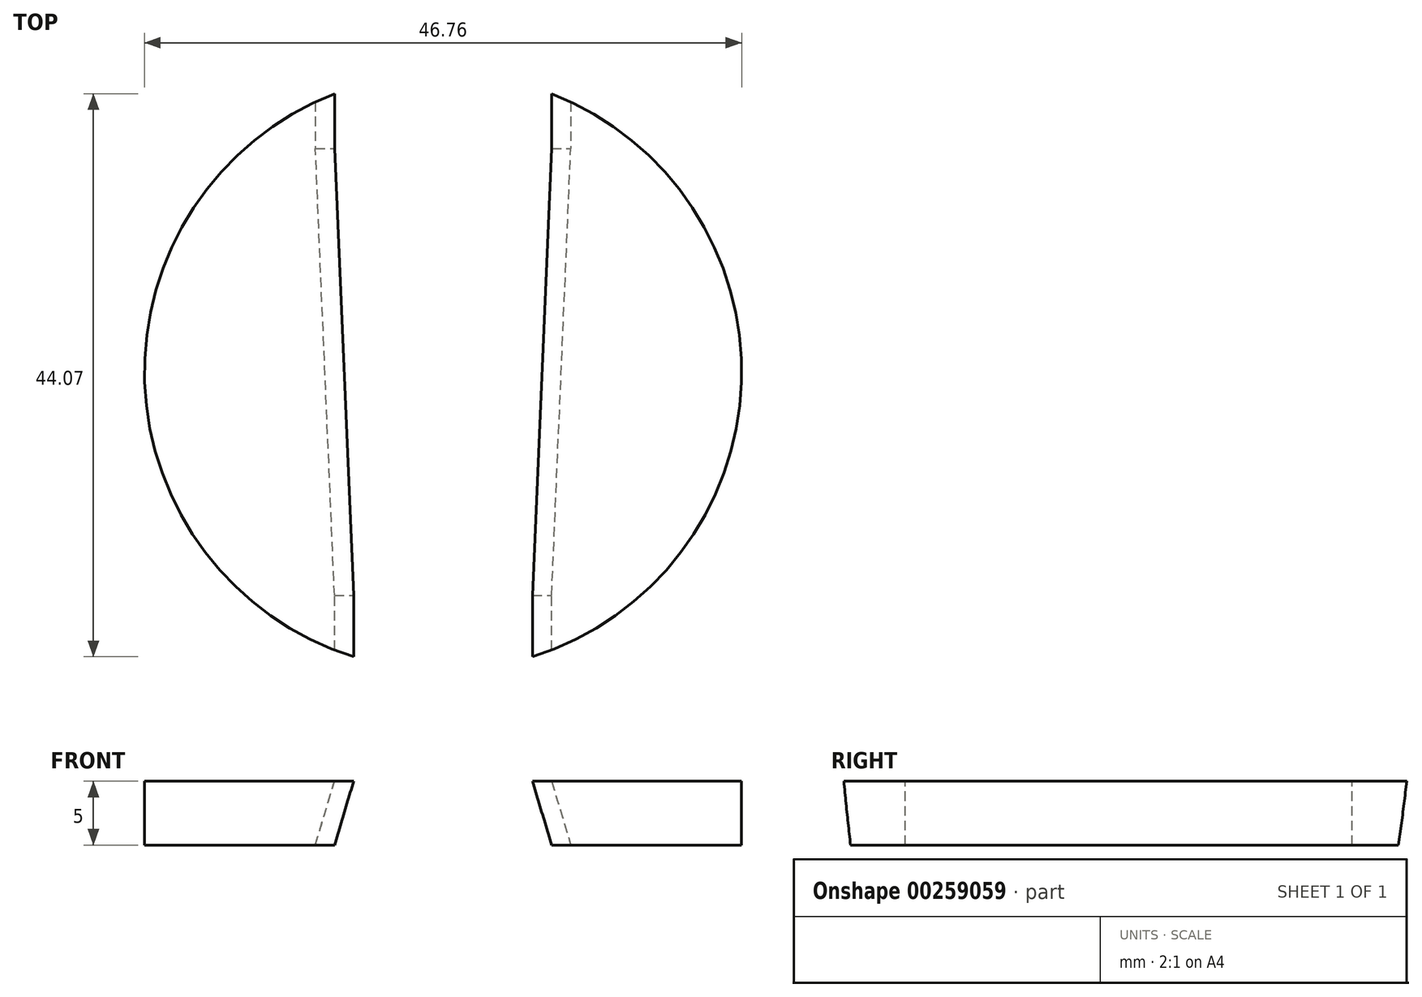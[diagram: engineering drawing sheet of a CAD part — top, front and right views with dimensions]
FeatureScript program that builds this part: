
annotation { "Feature Type Name" : "Feature", "Feature Type Description" : "" }
export const myFeature = defineFeature(function(context is Context, id is Id, definition is map)
    precondition{}
    {
        {
            var Q0;
            Q0=qCreatedBy(makeId("Top.planeOp"),FACE);
            var sketch = newSketch(context, id + "F0", { "sketchPlane" : qUnion([Q0])});
            skCircle(sketch, "E0", {"center": v(0, 0) * mm, "radius": 23.38 * mm});
            skSolve(sketch);
        }
        {
            var Q0;
            Q0=makeQuery(id+"F0.imprint","IMPRINT",FACE,{"disambiguationData":[TD([[makeQuery(id+"F0.imprint","IMPRINT",EDGE,{"derivedFrom":sQuery(id+"F0.wireOp",EDGE,"E0")}),1.0]])]});
            extrude(context, id + "F1", {"entities" : qUnion([Q0]), "depth" : 5 * mm, "offsetDistance" : 25 * mm});
        }
        {
            var Q0;
            Q0=qCreatedBy(makeId("Front.planeOp"),FACE);
            cPlane(context, id + "F2", {"entities" : qUnion([Q0]), "cplaneType" : CPlaneType.OFFSET, "offset" : (35 / 2) * mm, "width" : 150 * mm, "height" : 150 * mm});
        }
        {
            var Q0;
            Q0=qCreatedBy(makeId("Front.planeOp"),FACE);
            cPlane(context, id + "F3", {"entities" : qUnion([Q0]), "cplaneType" : CPlaneType.OFFSET, "offset" : (35 / 2) * mm, "oppositeDirection" : true, "width" : 150 * mm, "height" : 150 * mm});
        }
        {
            var Q0;
            Q0=qCreatedBy(id+"F2.planeOp",FACE);
            var sketch = newSketch(context, id + "F4", { "sketchPlane" : qUnion([Q0])});
            skLineSegment(sketch, "E1", {"start": v(-8.5, 0) * mm, "end": v(-7, 5) * mm});
            skLineSegment(sketch, "E2", {"start": v(-7, 5) * mm, "end": v(7, 5) * mm});
            skLineSegment(sketch, "E3", {"start": v(7, 5) * mm, "end": v(8.5, 0) * mm});
            skLineSegment(sketch, "E4", {"start": v(8.5, 0) * mm, "end": v(-8.5, 0) * mm});
            skPoint(sketch, "E5", {"position": v(0, 5) * mm});
            skPoint(sketch, "E6", {"position": v(0, 0) * mm});
            skSolve(sketch);
        }
        {
            var Q0;
            Q0=qCreatedBy(id+"F3.planeOp",FACE);
            var sketch = newSketch(context, id + "F5", { "sketchPlane" : qUnion([Q0])});
            skLineSegment(sketch, "E7", {"start": v(10, 0) * mm, "end": v(-10, 0) * mm});
            skLineSegment(sketch, "E8", {"start": v(-10, 0) * mm, "end": v(-8.5, 5) * mm});
            skLineSegment(sketch, "E9", {"start": v(-8.5, 5) * mm, "end": v(8.5, 5) * mm});
            skLineSegment(sketch, "E10", {"start": v(8.5, 5) * mm, "end": v(10, 0) * mm});
            skPoint(sketch, "E11", {"position": v(0, 5) * mm});
            skPoint(sketch, "E12", {"position": v(0, 0) * mm});
            skSolve(sketch);
        }
        {
            var Q1;
            Q1 = qSketchRegion(id + "F4", true);
            var Q2;
            Q2 = qSketchRegion(id + "F5", true);
            loft(context, id + "F6", {"operationType" : NewBodyOperationType.REMOVE, "sheetProfilesArray" : [{ "sheetProfileEntities" : qUnion([Q1]) }, { "sheetProfileEntities" : qUnion([Q2]) }]});
        }
        {
            var Q0;
            Q0 = qSketchRegion(id + "F4", true);
            extrude(context, id + "F7", {"entities" : qUnion([Q0]), "operationType" : NewBodyOperationType.REMOVE, "depth" : 25 * mm, "offsetDistance" : 25 * mm});
        }
        {
            var Q0;
            Q0 = qSketchRegion(id + "F5", true);
            extrude(context, id + "F8", {"entities" : qUnion([Q0]), "operationType" : NewBodyOperationType.REMOVE, "oppositeDirection" : true, "depth" : 25 * mm, "offsetDistance" : 25 * mm});
        }
    });
